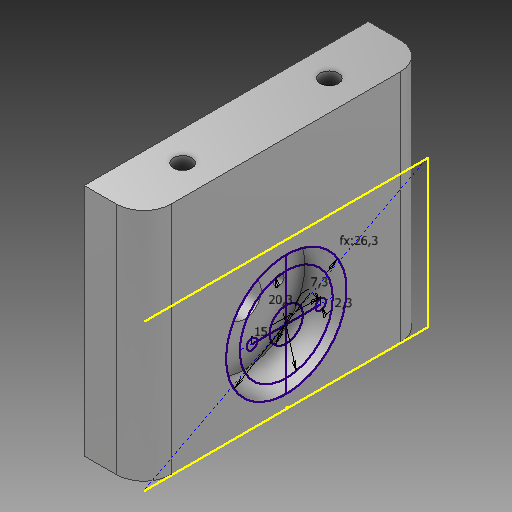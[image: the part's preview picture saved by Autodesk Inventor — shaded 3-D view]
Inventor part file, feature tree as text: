
AUTODESK INVENTOR PART (.ipt)
format: ipt  version: 2020 (Build 240168000, 168)  size: 213,504 bytes
history: native  units: mm
features: extrude x6, sketch x5, other x1, fillet x1, chamfer x1, projected_geometry x1
ambient origin geometry x8: Origin, YZ Plane, XZ Plane, XY Plane, X Axis, Y Axis, Z Axis, Center Point
bodies: Body1 (feature_tree)
feature tree (15):
  other  "Твердое тело1"
  extrude  "Выдавливание1"  Depth=13.0mm
  sketch  "Эскиз2"
  extrude  "Выдавливание3"  Depth=62.0mm
  extrude  "Выдавливание4"  Depth=16.0mm
  extrude  "Выдавливание5"  Depth=4.0mm
  fillet  "Сопряжение1"  [1 undecoded]
  chamfer  "Фаска1"  Distance=20.3mm
  extrude  "Выдавливание6"  Depth=2.3mm
  extrude  "Выдавливание7"  Depth=15.0mm
  sketch  "Эскиз1"
  sketch  "Эскиз3"
  sketch  "Эскиз6"
  projected_geometry  "Спроецированная петля2"
  sketch  "Эскиз7"
note: 1 required parameter value undecoded (feature->parameter linkage not recoverable at this tier; creation-order binding heuristic only, values carry confidence <= 0.55)
